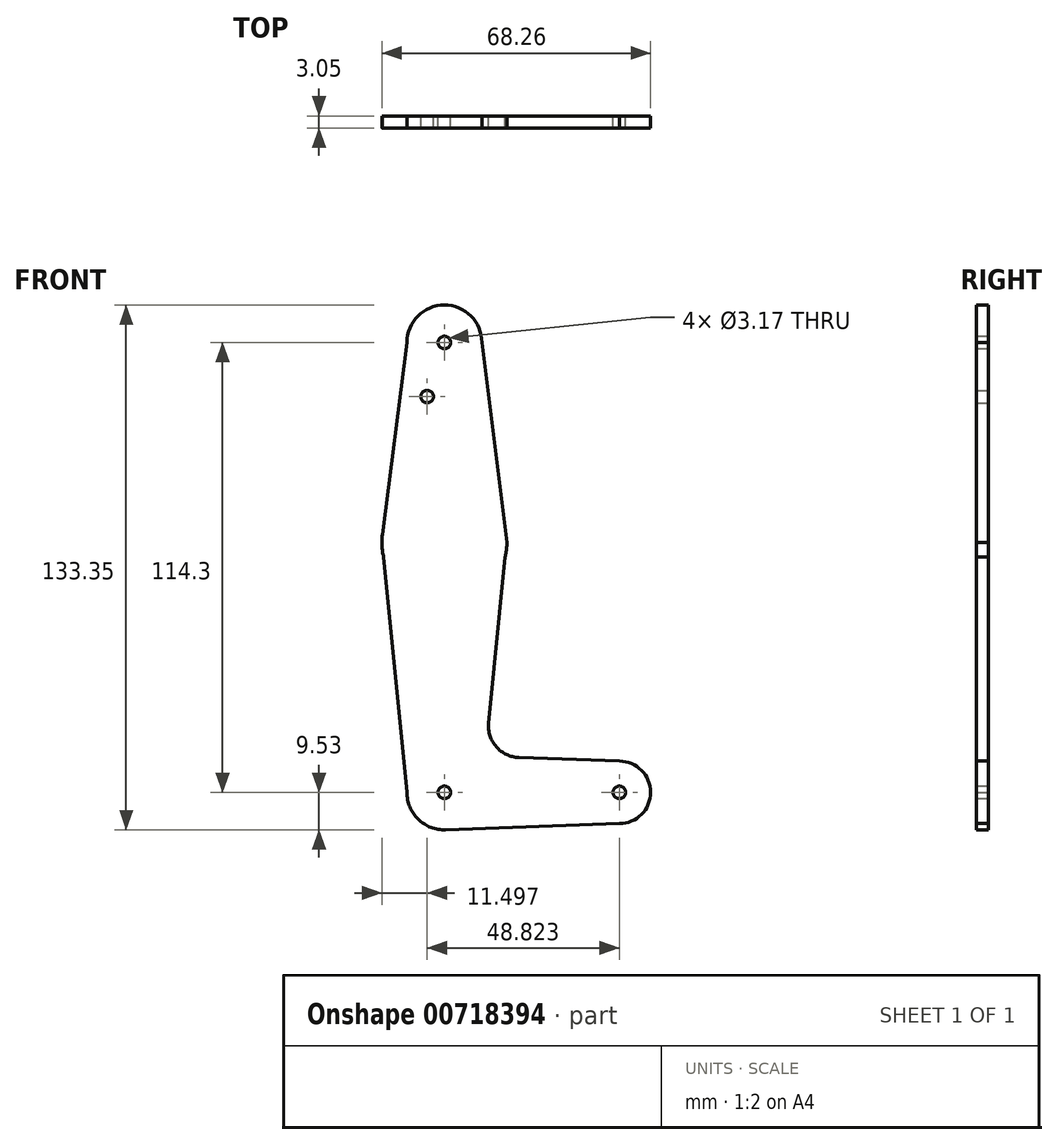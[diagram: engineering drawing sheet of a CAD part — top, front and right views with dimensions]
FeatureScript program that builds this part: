
annotation { "Feature Type Name" : "Feature", "Feature Type Description" : "" }
export const myFeature = defineFeature(function(context is Context, id is Id, definition is map)
    precondition{}
    {
        {
            var Q0;
            Q0=qCreatedBy(makeId("Front.planeOp"),FACE);
            var sketch = newSketch(context, id + "F0", { "sketchPlane" : qUnion([Q0])});
            skArc(sketch, "E0", {"start": v(-15.75, 2) * mm, "mid": v(-15.85, -0.86) * mm, "end": v(-15.44, -3.7) * mm});
            skArc(sketch, "E1", {"start": v(9.53, 50.8) * mm, "mid": v(0, 60.33) * mm, "end": v(-9.53, 50.8) * mm});
            skArc(sketch, "E2", {"start": v(-9.53, -63.5) * mm, "mid": v(-6.61, -70.35) * mm, "end": v(0.34, -73.02) * mm});
            skArc(sketch, "E3", {"start": v(44.45, -71.44) * mm, "mid": v(52.39, -63.5) * mm, "end": v(44.45, -55.56) * mm});
            skLineSegment(sketch, "E4", {"start": v(-9.53, 50.8) * mm, "end": v(-15.75, 2) * mm});
            skLineSegment(sketch, "E5", {"start": v(9.52, 50.8) * mm, "end": v(15.88, 0) * mm});
            skLineSegment(sketch, "E6", {"start": v(15.44, -3.7) * mm, "end": v(11.26, -45.92) * mm});
            skLineSegment(sketch, "E7", {"start": v(-15.44, -3.7) * mm, "end": v(-9.52, -63.5) * mm});
            skLineSegment(sketch, "E8", {"start": v(44.45, -55.56) * mm, "end": v(18.9, -54.65) * mm});
            skLineSegment(sketch, "E9", {"start": v(44.45, -71.44) * mm, "end": v(0, -73.03) * mm});
            skCircle(sketch, "E10", {"center": v(0, 50.8) * mm, "radius": 1.59 * mm});
            skCircle(sketch, "E11", {"center": v(0, -63.5) * mm, "radius": 1.59 * mm});
            skCircle(sketch, "E12", {"center": v(44.45, -63.5) * mm, "radius": 1.59 * mm});
            skCircle(sketch, "E13", {"center": v(-4.37, 37.06) * mm, "radius": 1.59 * mm});
            skPoint(sketch, "E14.newPointB", {"position": v(0, -53.97) * mm});
            skArc(sketch, "E14.filletArc", {"start": v(11.26, -45.92) * mm, "mid": v(13.19, -51.93) * mm, "end": v(18.9, -54.65) * mm});
            skArc(sketch, "E15.trimOffspring", {"start": v(15.44, -3.7) * mm, "mid": v(15.87, 0.1) * mm, "end": v(15.39, 3.9) * mm});
            skPoint(sketch, "E16.orphan", {"position": v(-16, 0) * mm});
            skSolve(sketch);
        }
        {
            var Q0;
            Q0=makeQuery(id+"F0.imprint","IMPRINT",FACE,{"disambiguationData":[TD([[makeQuery(id+"F0.imprint","IMPRINT",EDGE,{"derivedFrom":sQuery(id+"F0.wireOp",EDGE,"E0")}),1.0]])]});
            extrude(context, id + "F1", {"entities" : qUnion([Q0]), "depth" : 3.05 * mm, "offsetDistance" : 25.4 * mm});
        }
    });
